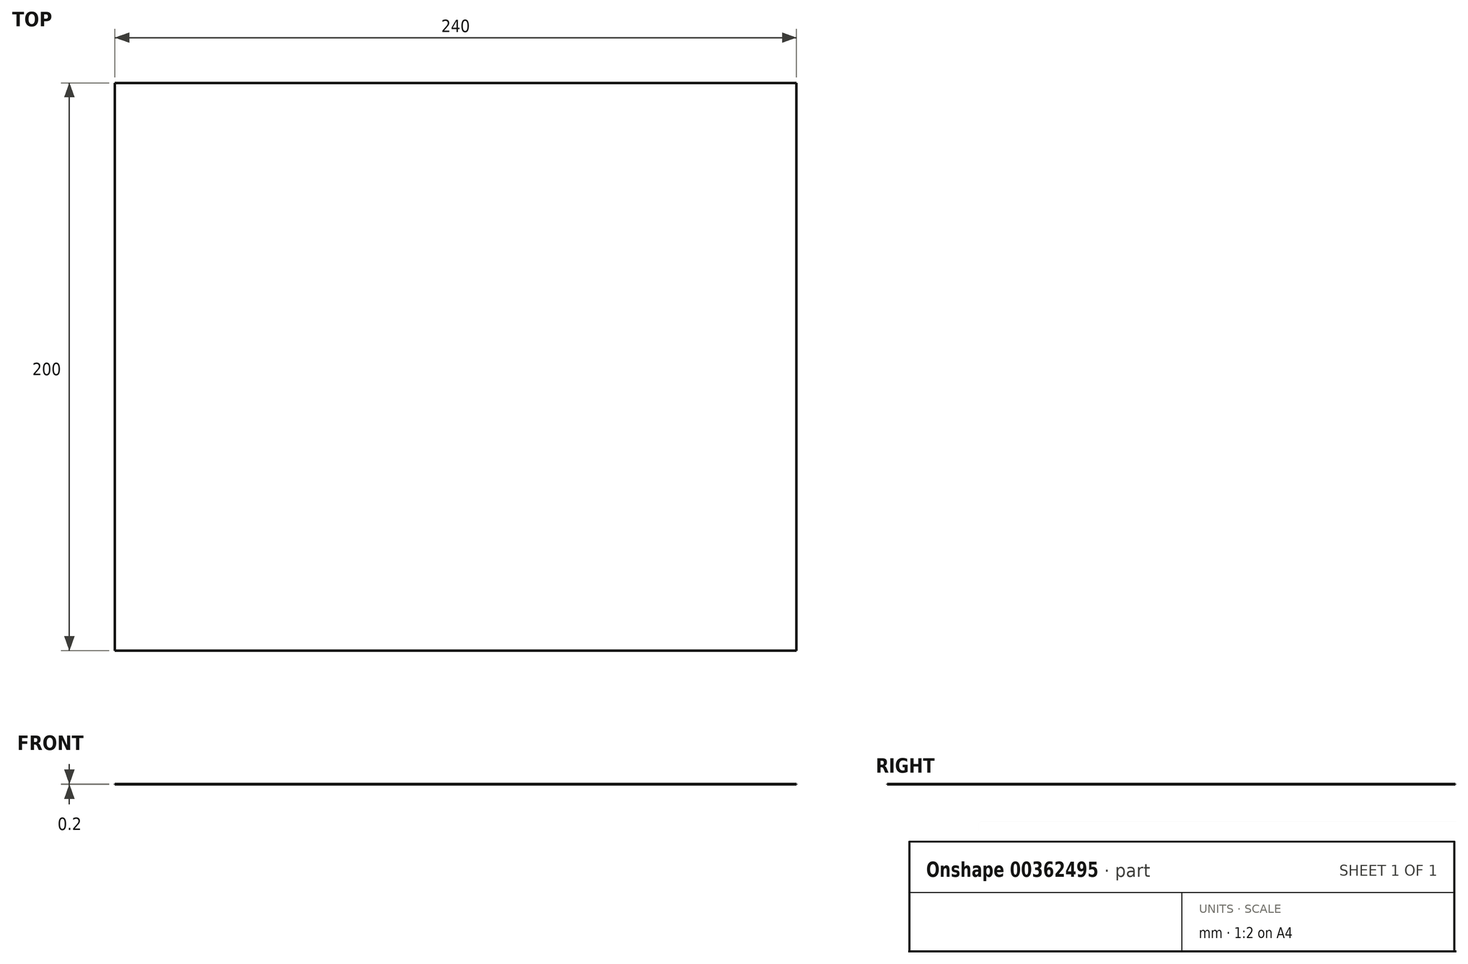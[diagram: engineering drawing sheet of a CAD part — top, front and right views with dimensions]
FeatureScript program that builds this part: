
annotation { "Feature Type Name" : "Feature", "Feature Type Description" : "" }
export const myFeature = defineFeature(function(context is Context, id is Id, definition is map)
    precondition{}
    {
        {
            var Q0;
            Q0=qCreatedBy(makeId("Top.planeOp"),FACE);
            var sketch = newSketch(context, id + "F0", { "sketchPlane" : qUnion([Q0])});
            skLineSegment(sketch, "E0.bottom", {"start": v(120, -100) * mm, "end": v(-120, -100) * mm});
            skLineSegment(sketch, "E0.top", {"start": v(120, 100) * mm, "end": v(-120, 100) * mm});
            skLineSegment(sketch, "E0.left", {"start": v(120, -100) * mm, "end": v(120, 100) * mm});
            skLineSegment(sketch, "E0.right", {"start": v(-120, -100) * mm, "end": v(-120, 100) * mm});
            skPoint(sketch, "E0.middle", {"position": v(0, 0) * mm});
            skSolve(sketch);
        }
        {
            var Q0;
            Q0=makeQuery(id+"F0.imprint","IMPRINT",FACE,{"disambiguationData":[TD([[makeQuery(id+"F0.imprint","IMPRINT",EDGE,{"derivedFrom":sQuery(id+"F0.wireOp",EDGE,"E0.bottom")}),-1.0]])]});
            extrude(context, id + "F1", {"entities" : qUnion([Q0]), "depth" : 0.2 * mm});
        }
    });
